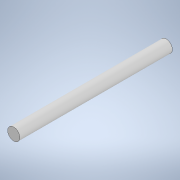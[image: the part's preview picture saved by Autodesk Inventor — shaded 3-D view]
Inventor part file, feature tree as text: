
AUTODESK INVENTOR PART (.ipt)
format: ipt  version: 2021 (Build 250183000, 183)  size: 92,672 bytes
history: native  units: in
note: dims shown in document units (in); Inventor stores cm internally (conversion verified against a paired STEP export)
features: sketch x2, extrude x1
ambient origin geometry x8: Origin, YZ Plane, XZ Plane, XY Plane, X Axis, Y Axis, Z Axis, Center Point
bodies: Body1 (feature_tree)
feature tree (3):
  sketch  "Sketch1"  dims[d20=1.5748in d21=19.685in d22=0.0in]
  extrude  "Extrusion3"  Depth=19.685in TaperAngle=0.0deg
  sketch  "Sketch5"  dims[d7=0.0197in d8=0.0344in d9=0.0197in d10=0.0344in]
